# Revit family: Maxima PSM 3G, Ø 20- Ø 46
name_source: partatom
category: HLS-Bauteile
units: mm (PartAtom-declared; Revit-internal decimal feet)

## family parameters
Arbeitsebenenbasiert = Ja
Beim Laden mit Abzugskörper schneiden = Nein
Bemaßung runder Anschluss = Durchmesser verwenden
Beschriftungsausrichtung beibehalten = Nein
Gemeinsam genutzt = Ja
Immer vertikal = Nein
Raumberechnungspunkt = Nein
Teiletyp = Normal

## types (5) — shared parameters
A = 18 mm  [stored 0.0590551 ft]
Anschluss = M8/M10 + 1/2''
Anschlußhöhe = 23 mm
Bauart = zweiteilig
Breite Material = 25 mm
DF1 = 23 mm  [stored 0.0754593 ft]
DF2 = 23 mm  [stored 0.0754593 ft]
DVS = 15 mm  [stored 0.0492126 ft]
Fabrikat = MEFA
Firma = MEFA Befestigungs- und Montagesysteme GmbH
HGA = 15 mm  [stored 0.0492126 ft]
Kurztext1 = Rohrschelle Maxima PSM 3G 25x3
MB = 25 mm  [stored 0.082021 ft]
MD = 3 mm  [stored 0.00984252 ft]
Material = Stahl
Materialmaße = 25x3,0 mm
Materialname = S235
Mengeneinheit = St
Oberflaeche = galvanisch verzinkt
Rohraußendurchmesser Zoll = 23 mm
Schalldämmeinlage = ohne Dämmung
Stärke Material = 3 mm  [stored 0.00984252 ft]
Verschluss = Pendelsteckmuttern
Verschluss-Schraube = M8
Vorgabe-Ansicht = 1219 mm
max. zul. Last = 0.70 kN
max. zul. Last horizontal = 0.00 kN
max. zul. Last vertikal = 0.00 kN
vpe = 1
zero-valued in all types: Nennweite DN Rohr, Rohraußendurchmesser

## per-type parameters (varying)
| type | AB | Achsabstand | Artikelnummer | B | Breite | D | Dmax | Dmin | EAN | Gewicht | Gewicht pro Bauteil | H | Kurztext2 | R | RM | S | max. Höhe | max. Rohraußendurchmesser | min. Höhe | min. Rohraußendurchmesser |
| Maxima PSM 3G, M8/M10-1/2", Ø 20- 23 | 3 mm  [stored 0.00984252 ft] | 49 mm | 0069047 | 75 mm  [stored 0.246063 ft] | 73 mm  [stored 0.239501 ft] | 23 mm  [stored 0.0754593 ft] | 23 mm  [stored 0.0754593 ft] | 20 mm  [stored 0.0656168 ft] | 4250928402684 | 0.22 kg | 0.22 kg | 44 mm  [stored 0.144357 ft] | 20 - 23 mm M8/M10 + 1/2'' o. Dämm. | 12 mm  [stored 0.0393701 ft] | 15 mm  [stored 0.0492126 ft] | 52 mm  [stored 0.170604 ft] | 44 mm  [stored 0.144357 ft] | 23 mm  [stored 0.0754593 ft] | 41 mm  [stored 0.134514 ft] | 20 mm  [stored 0.0656168 ft] |
| Maxima PSM 3G, M8/M10-1/2", Ø 25- 29 | 4 mm  [stored 0.0131234 ft] | 56 mm | 0069049 | 81 mm  [stored 0.265748 ft] | 80 mm  [stored 0.262467 ft] | 29 mm  [stored 0.0951444 ft] | 29 mm  [stored 0.0951444 ft] | 25 mm  [stored 0.082021 ft] | 4250928402691 | 0.23 kg | 0.23 kg | 50 mm  [stored 0.164042 ft] | 25 - 29 mm M8/M10 + 1/2'' o. Dämm. | 15 mm  [stored 0.0492126 ft] | 18 mm  [stored 0.0590551 ft] | 58 mm  [stored 0.190289 ft] | 50 mm  [stored 0.164042 ft] | 29 mm  [stored 0.0951444 ft] | 46 mm  [stored 0.150919 ft] | 25 mm  [stored 0.082021 ft] |
| Maxima PSM 3G, M8/M10-1/2", Ø 30- 35 | 5 mm  [stored 0.0164042 ft] | 63 mm | 0069053 | 87 mm  [stored 0.285433 ft] | 87 mm  [stored 0.285433 ft] | 35 mm  [stored 0.114829 ft] | 35 mm  [stored 0.114829 ft] | 30 mm  [stored 0.0984252 ft] | 4250928402707 | 0.24 kg | 0.24 kg | 56 mm  [stored 0.183727 ft] | 30 - 35 mm M8/M10 + 1/2'' o. Dämm. | 18 mm  [stored 0.0590551 ft] | 21 mm | 64 mm  [stored 0.209974 ft] | 56 mm  [stored 0.183727 ft] | 35 mm  [stored 0.114829 ft] | 51 mm | 30 mm  [stored 0.0984252 ft] |
| Maxima PSM 3G, M8/M10-1/2", Ø 36- 40 | 4 mm  [stored 0.0131234 ft] | 68 mm | 0069081 | 92 mm  [stored 0.301837 ft] | 92 mm  [stored 0.301837 ft] | 40 mm  [stored 0.131234 ft] | 40 mm  [stored 0.131234 ft] | 36 mm  [stored 0.11811 ft] | 4250928402721 | 0.25 kg | 0.25 kg | 61 mm  [stored 0.200131 ft] | 36 - 40 mm M8/M10 + 1/2'' o. Dämm. | 20 mm  [stored 0.0656168 ft] | 23 mm  [stored 0.0754593 ft] | 69 mm  [stored 0.226378 ft] | 61 mm  [stored 0.200131 ft] | 40 mm  [stored 0.131234 ft] | 57 mm  [stored 0.187008 ft] | 36 mm  [stored 0.11811 ft] |
| Maxima PSM 3G, M8/M10-1/2", Ø 41- 46 | 5 mm  [stored 0.0164042 ft] | 74 mm | 0069097 | 98 mm  [stored 0.321522 ft] | 98 mm  [stored 0.321522 ft] | 46 mm  [stored 0.150919 ft] | 46 mm  [stored 0.150919 ft] | 41 mm  [stored 0.134514 ft] | 4250928402738 | 0.26 kg | 0.26 kg | 67 mm | 41 - 46 mm M8/M10 + 1/2'' o. Dämm. | 23 mm  [stored 0.0754593 ft] | 26 mm  [stored 0.0853018 ft] | 75 mm  [stored 0.246063 ft] | 67 mm | 46 mm  [stored 0.150919 ft] | 62 mm  [stored 0.203412 ft] | 41 mm  [stored 0.134514 ft] |

note: [stored X ft] marks values corroborated as IEEE doubles in the binary element streams (Revit-internal decimal feet)

## geometry (parser evidence)
native form markers: Sweep x3
no freeform markers — native parametric forms only
